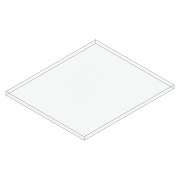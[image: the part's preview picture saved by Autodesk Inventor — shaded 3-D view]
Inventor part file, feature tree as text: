
AUTODESK INVENTOR PART (.ipt)
format: ipt  version: 2020.3 (Build 243373010, 373A)  size: 75,264 bytes
history: native  units: mm
features: extrude x1, sketch x1
ambient origin geometry x8: Origin, YZ Plane, XZ Plane, XY Plane, X Axis, Y Axis, Z Axis, Center Point
bodies: Solid1 (feature_tree)
feature tree (2):
  extrude  "Extrusion1"  Depth=110.0mm
  sketch  "Sketch1"  dims[d0=95.95mm d1=110.0mm d2=4.0mm d3=0.0mm]
